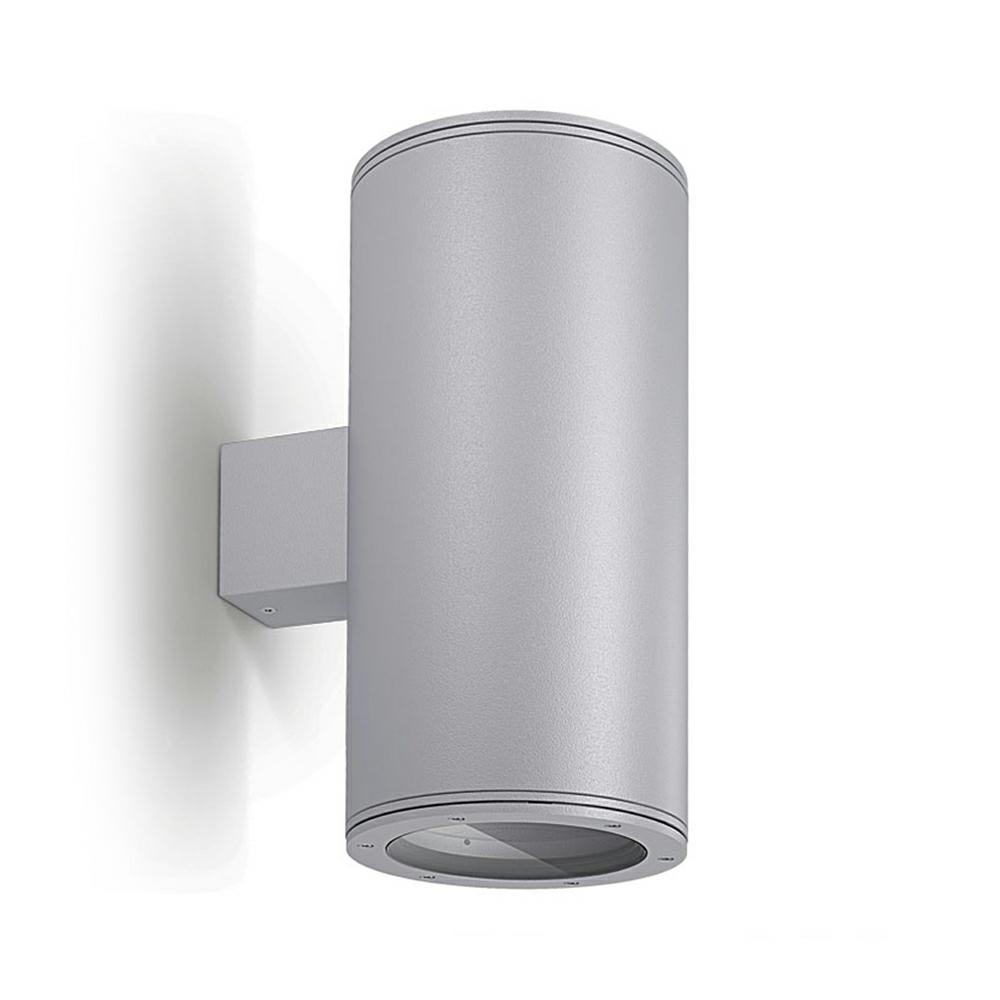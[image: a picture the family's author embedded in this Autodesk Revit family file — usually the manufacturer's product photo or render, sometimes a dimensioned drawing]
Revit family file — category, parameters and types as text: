
# Revit family: Platek_Monaco_200_Applique_2_Openings
name_source: partatom
category: Apparecchi per illuminazione
revit_build: Autodesk Revit 2018 (Build: 20170223_1515(x64)
units: mm (PartAtom-declared; Revit-internal decimal feet)

## family parameters
Basato su piano di lavoro = No
Condiviso = No
Punto di calcolo locali = No
Quota connettore circolare = Usa diametro
Sempre verticale = Sì
Sorgente d'illuminazione = No
Taglio con vuoti quando caricato = No
Tipo di parte = Normale

## types (2) — shared parameters
Body = PLK_06_Grey
CRI = >80
Colour Temprature = 3000 K
Commenti sul tipo = Facades, Wall
Descrizione = Outdoor Lighting, Wall mounted
Diffuse Type = Transparent Glass
Dimmable = NO
Energy Efficiency Rating = A/A+/A++
Frequency = 50/60 Hz
Glass = PLK_Light Source
IK Rating = IK10
IP Rating = IP65
Immagine tipo = monaco_200_applique.jpg
Inside Body = PLK_Optic
Insulation Class = 1
LED Protection = Surge protection included
Lampada = LED
Luminaire Wattage = 42 W
Manufacturer Comment = 2 Openings
Modello = Monaco 200 1Opening
Mounting Type = Wall
Nota chiave = Other LED colors available on request
Power Supply Unit = Included
Product Dimension = L280mm x L200mm x 400mm
Product Documentation Link = https://www.platek.eu
Product Page URL = https://www.platek.eu
Produttore = PLATEK SRL
Supply Voltage = 230 V
Supply Voltage Max = 240 V
Supply Voltage Min = 220 V
URL = www.platek.eu

## per-type parameters (varying)
| type | Codice assieme | Luminaire Luminous Flux | Luminaure Luminous Intensity | PLATEK Article Code | PLK_Photometrics |
| 8443411_42W_LED_3000K | 8443411.02(White);  8443411.06(Grey); 8443411.01(Black);  8443411.08(Anthracite); 8443411.07(Corten);  8443411.09(Bronze) | 3870 lm | 39086 cd | 8443411 | PLK_Photometrics : 8443411 |
| 8443418_42W_LED_3000K | 8443418.02(White);  8443418.06(Grey);  8443418.01(Black);  8443418.08(Anthracite); 8443418.07(Corten);  8443418.09(Bronze) | 3230 lm | 2230 cd | 8443418 | PLK_Photometrics : 8443418 |
